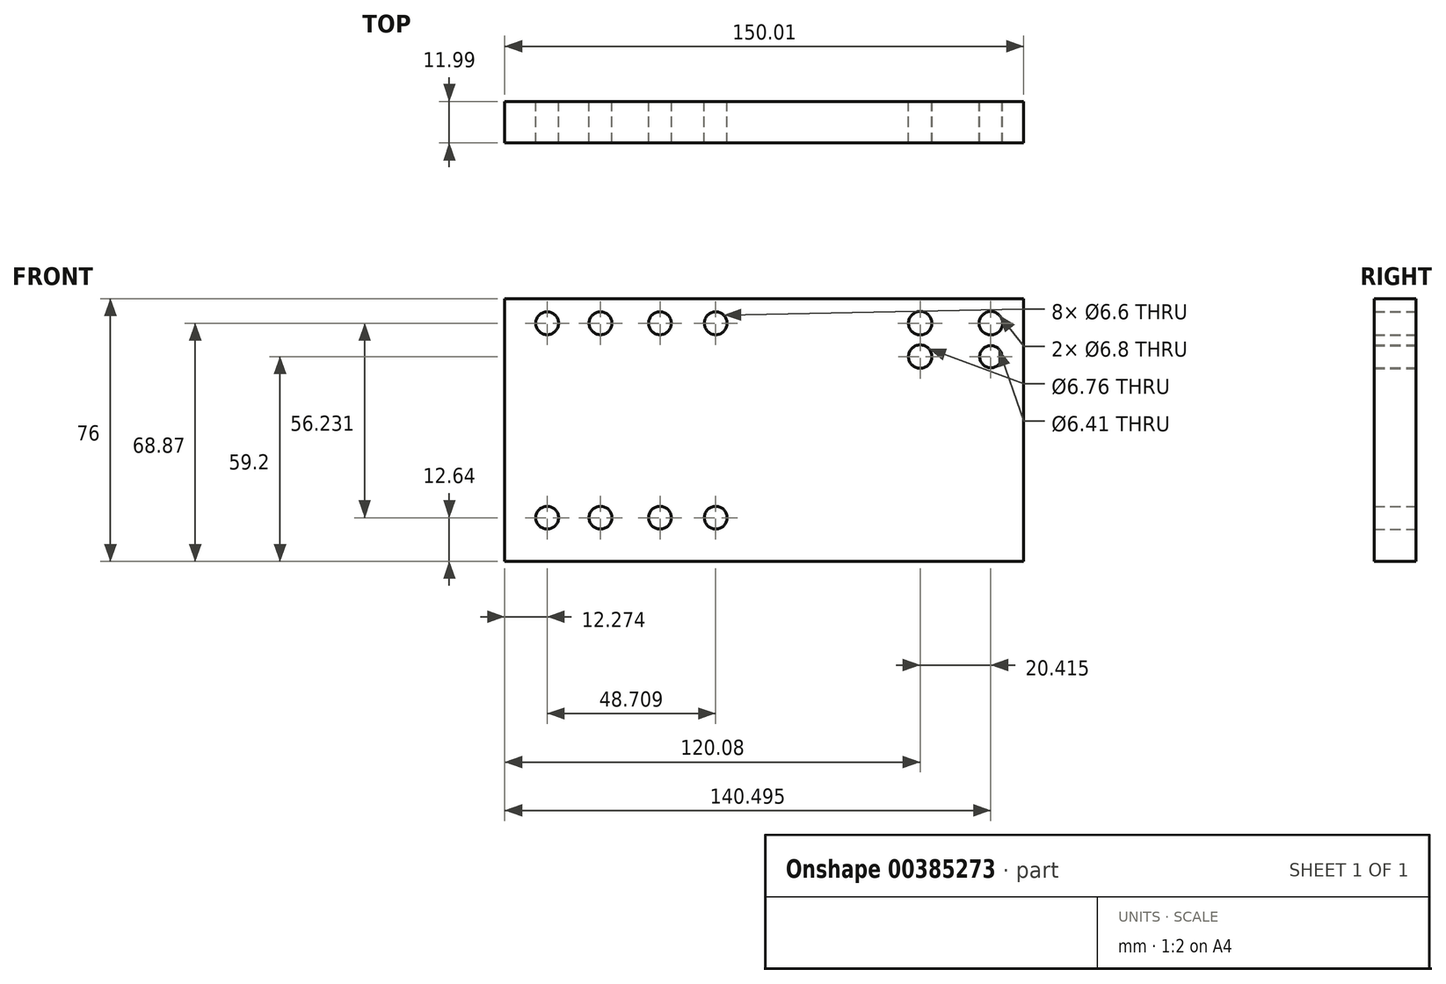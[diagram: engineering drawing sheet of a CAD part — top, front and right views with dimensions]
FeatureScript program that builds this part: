
annotation { "Feature Type Name" : "Feature", "Feature Type Description" : "" }
export const myFeature = defineFeature(function(context is Context, id is Id, definition is map)
    precondition{}
    {
        {
            var Q0;
            Q0=qCreatedBy(makeId("Front.planeOp"),FACE);
            var sketch = newSketch(context, id + "F0", { "sketchPlane" : qUnion([Q0])});
            skLineSegment(sketch, "E0", {"start": v(-57.12, 39.31) * mm, "end": v(92.89, 39.31) * mm});
            skLineSegment(sketch, "E1", {"start": v(92.89, 39.31) * mm, "end": v(92.89, -36.69) * mm});
            skLineSegment(sketch, "E2", {"start": v(92.89, -36.69) * mm, "end": v(-57.12, -36.69) * mm});
            skLineSegment(sketch, "E3", {"start": v(-57.12, 39.31) * mm, "end": v(-57.12, -31.97) * mm});
            skLineSegment(sketch, "E4", {"start": v(-57.12, -31.97) * mm, "end": v(-57.12, -36.69) * mm});
            skCircle(sketch, "E5", {"center": v(62.96, 32.18) * mm, "radius": 3.4 * mm});
            skCircle(sketch, "E6", {"center": v(83.37, 32.18) * mm, "radius": 3.4 * mm});
            skCircle(sketch, "E7", {"center": v(83.37, 22.51) * mm, "radius": 3.2 * mm});
            skCircle(sketch, "E8", {"center": v(62.96, 22.51) * mm, "radius": 3.38 * mm});
            skCircle(sketch, "E9", {"center": v(-44.85, 32.18) * mm, "radius": 3.3 * mm});
            skCircle(sketch, "E10", {"center": v(-29.45, 32.18) * mm, "radius": 3.3 * mm});
            skCircle(sketch, "E11", {"center": v(-12.25, 32.18) * mm, "radius": 3.3 * mm});
            skCircle(sketch, "E12", {"center": v(3.86, 32.18) * mm, "radius": 3.3 * mm});
            skCircle(sketch, "E13", {"center": v(-44.85, -24.05) * mm, "radius": 3.3 * mm});
            skCircle(sketch, "E14", {"center": v(-29.45, -24.05) * mm, "radius": 3.3 * mm});
            skCircle(sketch, "E15", {"center": v(-12.25, -24.05) * mm, "radius": 3.3 * mm});
            skCircle(sketch, "E16", {"center": v(3.86, -24.05) * mm, "radius": 3.3 * mm});
            skSolve(sketch);
        }
        {
            var Q0;
            Q0 = qSketchRegion(id + "F0", true);
            extrude(context, id + "F1", {"entities" : qUnion([Q0]), "depth" : 12 * mm});
        }
    });
